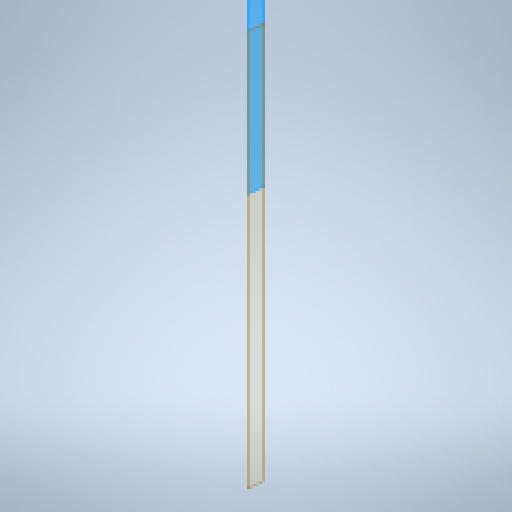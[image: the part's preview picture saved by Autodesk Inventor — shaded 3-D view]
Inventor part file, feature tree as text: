
AUTODESK INVENTOR PART (.ipt)
format: ipt  version: 2023 (Build 270158000, 158)  size: 142,336 bytes
history: native  units: mm
features: other x2, plane x1, extrude x1, sketch x1
ambient origin geometry x8: Origin, YZ Plane, XZ Plane, XY Plane, X Axis, Y Axis, Z Axis, Center Point
bodies: Solid1 (feature_tree)
feature tree (5):
  plane  "Work Plane2"
  extrude  "Extrusion1"  Depth=314.3mm
  sketch  "Sketch2"  dims[d0=314.3mm d1=314.3mm d2=10.0mm d3=0.0mm]
  other  "Assembly1"
  other  "wall:1"
